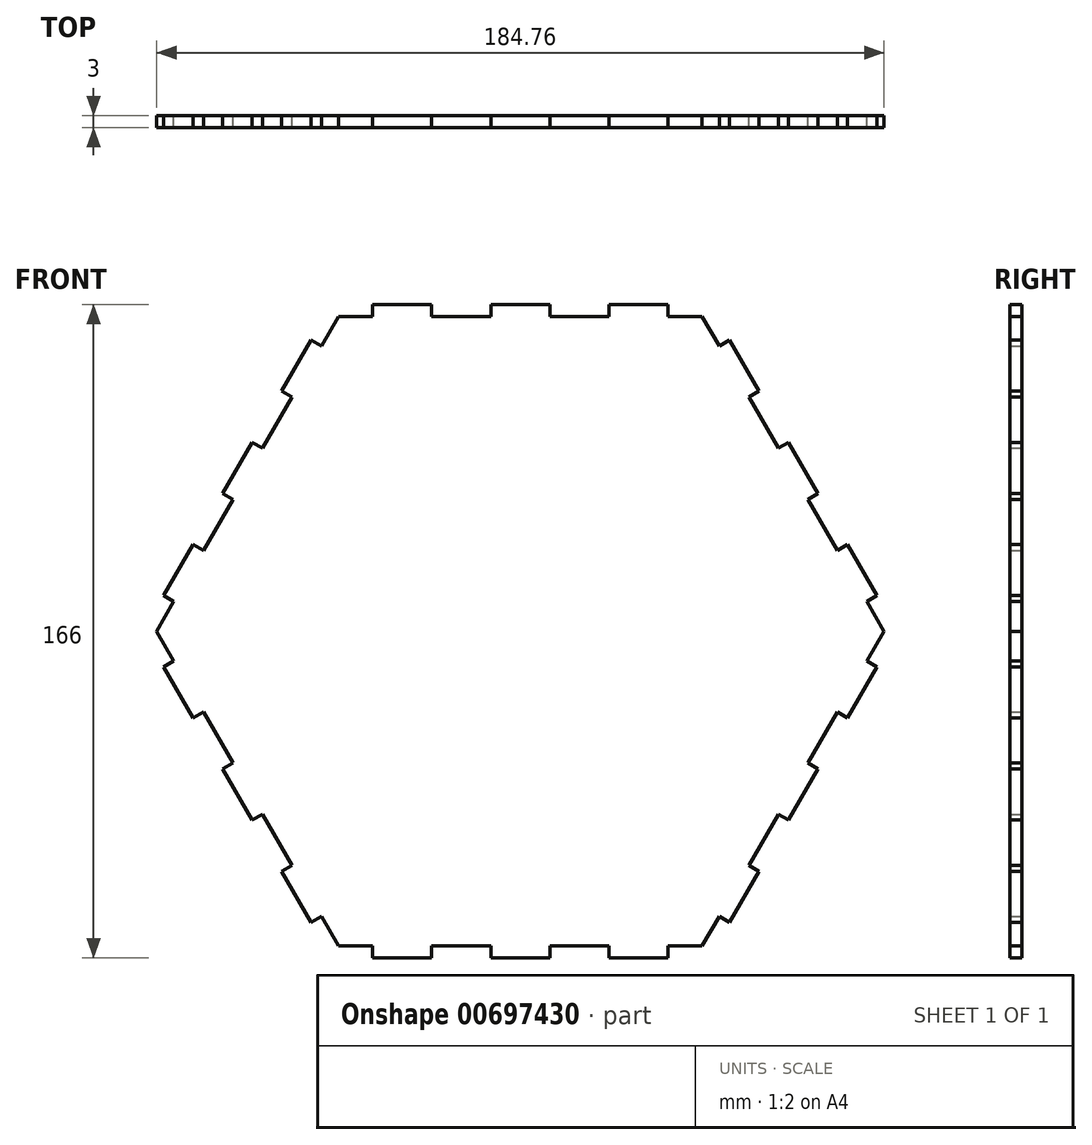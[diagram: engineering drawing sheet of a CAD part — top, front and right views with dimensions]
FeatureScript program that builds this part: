
annotation { "Feature Type Name" : "Feature", "Feature Type Description" : "" }
export const myFeature = defineFeature(function(context is Context, id is Id, definition is map)
    precondition{}
    {
        {
            var Q0;
            Q0=qCreatedBy(makeId("Front.planeOp"),FACE);
            var sketch = newSketch(context, id + "F0", { "sketchPlane" : qUnion([Q0])});
            skLineSegment(sketch, "E0.0", {"start": v(-46.19, 80) * mm, "end": v(-37.5, 80) * mm});
            skLineSegment(sketch, "E0.1", {"start": v(46.19, 80) * mm, "end": v(50.53, 72.48) * mm});
            skLineSegment(sketch, "E0.2", {"start": v(92.38, 0) * mm, "end": v(88.03, -7.52) * mm});
            skLineSegment(sketch, "E0.3", {"start": v(46.19, -80) * mm, "end": v(37.5, -80) * mm});
            skLineSegment(sketch, "E0.4", {"start": v(-46.19, -80) * mm, "end": v(-50.53, -72.48) * mm});
            skLineSegment(sketch, "E0.5", {"start": v(-92.38, 0) * mm, "end": v(-88.03, 7.52) * mm});
            skPoint(sketch, "E0.0.midPoint", {"position": v(0, 80) * mm});
            skLineSegment(sketch, "E1", {"start": v(-71.88, 41.5) * mm, "end": v(-68.13, 48) * mm});
            skLineSegment(sketch, "E2", {"start": v(-68.13, 48) * mm, "end": v(-65.53, 46.5) * mm});
            skLineSegment(sketch, "E3", {"start": v(-58.03, 59.49) * mm, "end": v(-60.63, 60.99) * mm});
            skLineSegment(sketch, "E4", {"start": v(-53.13, 73.98) * mm, "end": v(-50.53, 72.48) * mm});
            skLineSegment(sketch, "E5.trimOffspring", {"start": v(-60.63, 60.99) * mm, "end": v(-53.13, 73.98) * mm});
            skLineSegment(sketch, "E6.trimOffspring", {"start": v(-65.53, 46.5) * mm, "end": v(-58.03, 59.49) * mm});
            skLineSegment(sketch, "E7.trimOffspring", {"start": v(-50.53, 72.48) * mm, "end": v(-46.19, 80) * mm});
            skLineSegment(sketch, "E8", {"start": v(-71.88, 41.5) * mm, "end": v(-75.63, 35) * mm});
            skLineSegment(sketch, "E9", {"start": v(-75.63, 35) * mm, "end": v(-73.03, 33.5) * mm});
            skLineSegment(sketch, "E10", {"start": v(-80.53, 20.51) * mm, "end": v(-83.13, 22.01) * mm});
            skLineSegment(sketch, "E11", {"start": v(-83.13, 22.01) * mm, "end": v(-90.63, 9.02) * mm});
            skLineSegment(sketch, "E12", {"start": v(-90.63, 9.02) * mm, "end": v(-88.03, 7.52) * mm});
            skLineSegment(sketch, "E13.trimOffspring", {"start": v(-80.53, 20.51) * mm, "end": v(-73.03, 33.5) * mm});
            skLineSegment(sketch, "E14.1.3", {"start": v(65.53, 46.5) * mm, "end": v(65.53, 46.5) * mm});
            skLineSegment(sketch, "E14.1.4", {"start": v(79.38, 38.5) * mm, "end": v(79.38, 38.5) * mm});
            skLineSegment(sketch, "E14.1.6", {"start": v(73.03, 33.5) * mm, "end": v(73.03, 33.5) * mm});
            skLineSegment(sketch, "E14.1.11", {"start": v(75.63, 57.99) * mm, "end": v(73.03, 59.49) * mm});
            skPoint(sketch, "E14.center", {"position": v(0, 0) * mm});
            skPoint(sketch, "E15.orphan", {"position": v(-47.88, 83.07) * mm});
            skLineSegment(sketch, "E16.1.0", {"start": v(-90.63, -9.02) * mm, "end": v(-88.03, -7.52) * mm});
            skLineSegment(sketch, "E16.1.1", {"start": v(-83.13, -22.01) * mm, "end": v(-90.63, -9.02) * mm});
            skLineSegment(sketch, "E16.1.2", {"start": v(-80.53, -20.51) * mm, "end": v(-83.13, -22.01) * mm});
            skLineSegment(sketch, "E16.1.3", {"start": v(-75.63, -35) * mm, "end": v(-73.03, -33.5) * mm});
            skLineSegment(sketch, "E16.1.4", {"start": v(-71.88, -41.5) * mm, "end": v(-75.63, -35) * mm});
            skLineSegment(sketch, "E16.1.5", {"start": v(-71.88, -41.5) * mm, "end": v(-68.13, -48) * mm});
            skLineSegment(sketch, "E16.1.6", {"start": v(-68.13, -48) * mm, "end": v(-65.53, -46.5) * mm});
            skLineSegment(sketch, "E16.1.7", {"start": v(-58.03, -59.49) * mm, "end": v(-60.63, -60.99) * mm});
            skLineSegment(sketch, "E16.1.8", {"start": v(-60.63, -60.99) * mm, "end": v(-53.13, -73.98) * mm});
            skLineSegment(sketch, "E16.1.9", {"start": v(-53.13, -73.98) * mm, "end": v(-50.53, -72.48) * mm});
            skLineSegment(sketch, "E16.2.0", {"start": v(-37.5, -83) * mm, "end": v(-37.5, -80) * mm});
            skLineSegment(sketch, "E16.2.1", {"start": v(-22.5, -83) * mm, "end": v(-37.5, -83) * mm});
            skLineSegment(sketch, "E16.2.2", {"start": v(-22.5, -80) * mm, "end": v(-22.5, -83) * mm});
            skLineSegment(sketch, "E16.2.3", {"start": v(-7.5, -83) * mm, "end": v(-7.5, -80) * mm});
            skLineSegment(sketch, "E16.2.4", {"start": v(0, -83) * mm, "end": v(-7.5, -83) * mm});
            skLineSegment(sketch, "E16.2.5", {"start": v(0, -83) * mm, "end": v(7.5, -83) * mm});
            skLineSegment(sketch, "E16.2.6", {"start": v(7.5, -83) * mm, "end": v(7.5, -80) * mm});
            skLineSegment(sketch, "E16.2.7", {"start": v(22.5, -80) * mm, "end": v(22.5, -83) * mm});
            skLineSegment(sketch, "E16.2.8", {"start": v(22.5, -83) * mm, "end": v(37.5, -83) * mm});
            skLineSegment(sketch, "E16.2.9", {"start": v(37.5, -83) * mm, "end": v(37.5, -80) * mm});
            skLineSegment(sketch, "E16.3.0", {"start": v(53.13, -73.98) * mm, "end": v(50.53, -72.48) * mm});
            skLineSegment(sketch, "E16.3.1", {"start": v(60.63, -60.99) * mm, "end": v(53.13, -73.98) * mm});
            skLineSegment(sketch, "E16.3.2", {"start": v(58.03, -59.49) * mm, "end": v(60.63, -60.99) * mm});
            skLineSegment(sketch, "E16.3.3", {"start": v(68.13, -48) * mm, "end": v(65.53, -46.5) * mm});
            skLineSegment(sketch, "E16.3.4", {"start": v(71.88, -41.5) * mm, "end": v(68.13, -48) * mm});
            skLineSegment(sketch, "E16.3.5", {"start": v(71.88, -41.5) * mm, "end": v(75.63, -35) * mm});
            skLineSegment(sketch, "E16.3.6", {"start": v(75.63, -35) * mm, "end": v(73.03, -33.5) * mm});
            skLineSegment(sketch, "E16.3.7", {"start": v(80.53, -20.51) * mm, "end": v(83.13, -22.01) * mm});
            skLineSegment(sketch, "E16.3.8", {"start": v(83.13, -22.01) * mm, "end": v(90.63, -9.02) * mm});
            skLineSegment(sketch, "E16.3.9", {"start": v(90.63, -9.02) * mm, "end": v(88.03, -7.52) * mm});
            skLineSegment(sketch, "E16.4.0", {"start": v(90.63, 9.02) * mm, "end": v(88.03, 7.52) * mm});
            skLineSegment(sketch, "E16.4.1", {"start": v(83.13, 22.01) * mm, "end": v(90.63, 9.02) * mm});
            skLineSegment(sketch, "E16.4.2", {"start": v(80.53, 20.51) * mm, "end": v(83.13, 22.01) * mm});
            skLineSegment(sketch, "E16.4.3", {"start": v(75.63, 35) * mm, "end": v(73.03, 33.5) * mm});
            skLineSegment(sketch, "E16.4.4", {"start": v(71.88, 41.5) * mm, "end": v(75.63, 35) * mm});
            skLineSegment(sketch, "E16.4.5", {"start": v(71.88, 41.5) * mm, "end": v(68.13, 48) * mm});
            skLineSegment(sketch, "E16.4.6", {"start": v(68.13, 48) * mm, "end": v(65.53, 46.5) * mm});
            skLineSegment(sketch, "E16.4.7", {"start": v(58.03, 59.49) * mm, "end": v(60.63, 60.99) * mm});
            skLineSegment(sketch, "E16.4.8", {"start": v(60.63, 60.99) * mm, "end": v(53.13, 73.98) * mm});
            skLineSegment(sketch, "E16.4.9", {"start": v(53.13, 73.98) * mm, "end": v(50.53, 72.48) * mm});
            skLineSegment(sketch, "E16.5.0", {"start": v(37.5, 83) * mm, "end": v(37.5, 80) * mm});
            skLineSegment(sketch, "E16.5.1", {"start": v(22.5, 83) * mm, "end": v(37.5, 83) * mm});
            skLineSegment(sketch, "E16.5.2", {"start": v(22.5, 80) * mm, "end": v(22.5, 83) * mm});
            skLineSegment(sketch, "E16.5.3", {"start": v(7.5, 83) * mm, "end": v(7.5, 80) * mm});
            skLineSegment(sketch, "E16.5.4", {"start": v(0, 83) * mm, "end": v(7.5, 83) * mm});
            skLineSegment(sketch, "E16.5.5", {"start": v(0, 83) * mm, "end": v(-7.5, 83) * mm});
            skLineSegment(sketch, "E16.5.6", {"start": v(-7.5, 83) * mm, "end": v(-7.5, 80) * mm});
            skLineSegment(sketch, "E16.5.7", {"start": v(-22.5, 80) * mm, "end": v(-22.5, 83) * mm});
            skLineSegment(sketch, "E16.5.8", {"start": v(-22.5, 83) * mm, "end": v(-37.5, 83) * mm});
            skLineSegment(sketch, "E16.5.9", {"start": v(-37.5, 83) * mm, "end": v(-37.5, 80) * mm});
            skLineSegment(sketch, "E17.trimOffspring", {"start": v(-88.03, -7.52) * mm, "end": v(-92.38, 0) * mm});
            skLineSegment(sketch, "E18.trimOffspring", {"start": v(-73.03, -33.5) * mm, "end": v(-80.53, -20.51) * mm});
            skLineSegment(sketch, "E19.trimOffspring", {"start": v(-58.03, -59.49) * mm, "end": v(-65.53, -46.5) * mm});
            skPoint(sketch, "E20.orphan", {"position": v(-42.75, -92.1) * mm});
            skLineSegment(sketch, "E21.trimOffspring", {"start": v(-37.5, -80) * mm, "end": v(-46.19, -80) * mm});
            skLineSegment(sketch, "E22.trimOffspring", {"start": v(-7.5, -80) * mm, "end": v(-22.5, -80) * mm});
            skLineSegment(sketch, "E23.trimOffspring", {"start": v(50.53, -72.48) * mm, "end": v(46.19, -80) * mm});
            skLineSegment(sketch, "E24.trimOffspring", {"start": v(80.53, -20.51) * mm, "end": v(73.03, -33.5) * mm});
            skLineSegment(sketch, "E25.trimOffspring", {"start": v(65.53, -46.5) * mm, "end": v(58.03, -59.49) * mm});
            skLineSegment(sketch, "E26.trimOffspring", {"start": v(88.03, 7.52) * mm, "end": v(92.38, 0) * mm});
            skLineSegment(sketch, "E27.trimOffspring", {"start": v(37.5, 80) * mm, "end": v(46.19, 80) * mm});
            skLineSegment(sketch, "E28.trimOffspring", {"start": v(-22.5, 80) * mm, "end": v(-7.5, 80) * mm});
            skLineSegment(sketch, "E29.trimOffspring", {"start": v(7.5, 80) * mm, "end": v(22.5, 80) * mm});
            skLineSegment(sketch, "E30", {"start": v(73.03, 33.5) * mm, "end": v(80.53, 20.51) * mm});
            skLineSegment(sketch, "E31", {"start": v(58.03, 59.49) * mm, "end": v(65.53, 46.5) * mm});
            skLineSegment(sketch, "E32", {"start": v(22.5, -80) * mm, "end": v(7.5, -80) * mm});
            skSolve(sketch);
        }
        {
            var Q0;
            Q0 = qSketchRegion(id + "F0", true);
            var Q1;
            Q1=makeQuery(id+"F0.imprint","IMPRINT",FACE,{"disambiguationData":[TD([[makeQuery(id+"F0.imprint","IMPRINT",EDGE,{"derivedFrom":sQuery(id+"F0.wireOp",EDGE,"E0.0")}),-1.0]])]});
            extrude(context, id + "F1", {"entities" : qUnion([Q0, Q1]), "depth" : 3 * mm, "offsetDistance" : 25 * mm});
        }
        {
            var Q0;
            Q0=qCreatedBy(makeId("Top.planeOp"),FACE);
            cPlane(context, id + "F2", {"entities" : qUnion([Q0]), "cplaneType" : CPlaneType.OFFSET, "offset" : 100 * mm, "width" : 150 * mm, "height" : 150 * mm});
        }
    });
